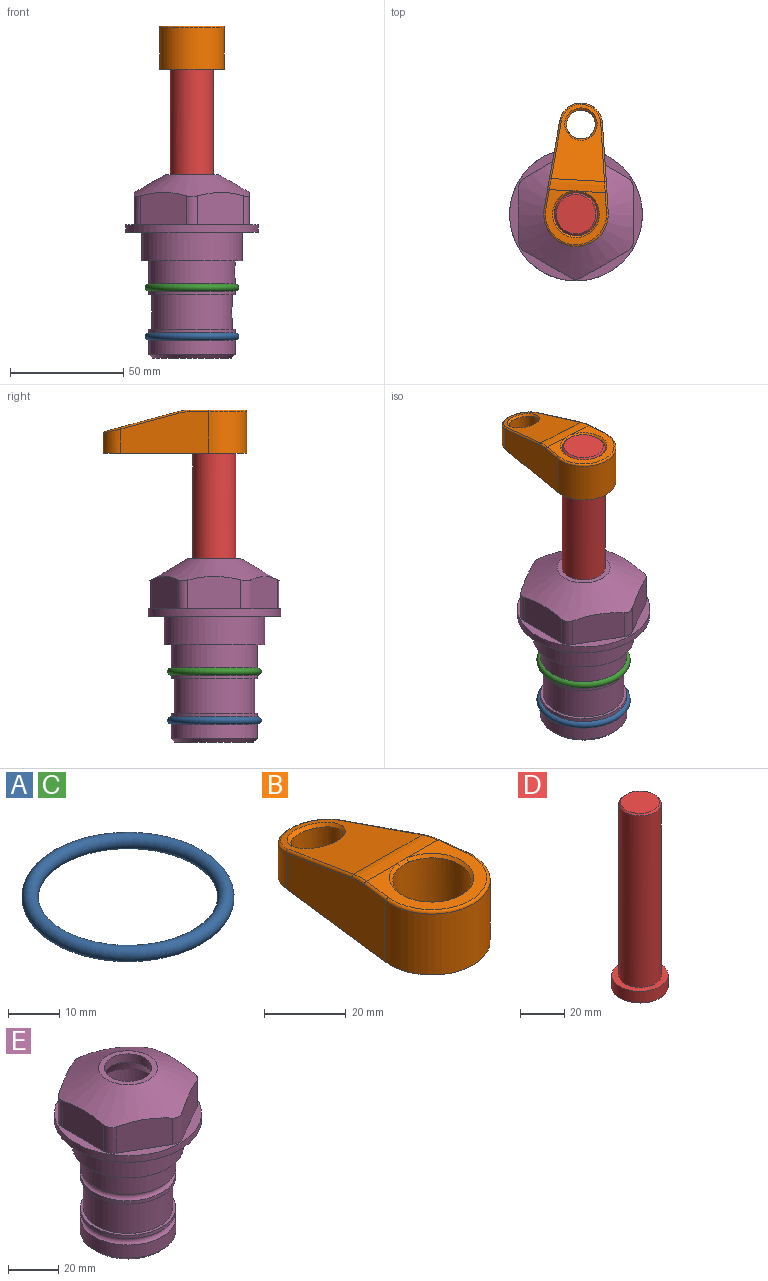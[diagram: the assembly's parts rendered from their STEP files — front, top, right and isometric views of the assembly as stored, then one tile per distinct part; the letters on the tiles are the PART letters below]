
ASSEMBLY  parts=5 mates=4
PART A: 1 faces, bbox 44.7x44.7x3.2 mm
  f0: torus R=19.05mm, axis (0,0,1), area 1193.9mm2
PART B: 31 faces, bbox 31.7x65.5x19.8 mm
  f0: plane 39.12x18.26mm, normal (0.99,0.12,0), area 612.2mm2, adj f1,f4,f7,f11,f13,f15
  f1: cylinder r=9.53mm len=18.91mm, axis (0,0,-1), area 296.1mm2, adj f0,f2,f7,f17
  f2: plane 39.12x18.26mm, normal (-0.99,0.12,0), area 612.2mm2, adj f1,f4,f7,f12,f14,f16
  f3: cylinder r=6.35mm len=12.7mm, axis (0,0,-1), area 362.4mm2, adj f7,f18
  f4: cylinder r=14.29mm len=28.58mm, axis (0,0,-1), area 882.2mm2, adj f0,f2,f7,f10
  f5: cylinder r=9.53mm len=19.05mm, axis (0,0,-1), area 1092.6mm2, adj f7,f19,f20
  f6: plane 26.99x23.69mm, normal (0,0,1), area 216.2mm2, adj f9,f10,f11,f12,f19
  f7: plane 63.5x28.58mm, normal (0,0,-1), area 661.8mm2, adj f0,f1,f2,f3,f4,f5,f22,f23
  f8: plane 33.52x23.6mm, normal (0,0.26,0.97), area 486mm2, adj f9,f15,f16,f17,f18
  f9: cylinder r=19.05mm len=24.72mm, axis (1,0,0), area 120.4mm2, adj f6,f8,f13,f14,f20
  f10: torus R=13.49mm, axis (0,0,1), area 59mm2, adj f4,f6,f11,f12
  f11: cylinder r=0.79mm len=8.67mm, axis (0.12,-0.99,0), area 10.8mm2, adj f0,f6,f10,f13
  f12: cylinder r=0.79mm len=8.67mm, axis (0.12,0.99,0), area 10.8mm2, adj f2,f6,f10,f14
  f13: bspline ~4.95x1.42mm, area 6.1mm2, adj f0,f9,f11,f15
  f14: bspline ~4.95x1.42mm, area 6.1mm2, adj f2,f9,f12,f16
  f15: cylinder r=0.79mm len=25.95mm, axis (0.12,-0.96,0.26), area 32.9mm2, adj f0,f8,f13,f17
  f16: cylinder r=0.79mm len=25.95mm, axis (0.12,0.96,-0.26), area 32.9mm2, adj f2,f8,f14,f17
  f17: bspline ~18.91x8.38mm, area 30mm2, adj f1,f8,f15,f16
  f18: bspline ~14.29x14.29mm, area 48.3mm2, adj f3,f8
  f19: cone r=9.53mm half-angle=45deg, axis (0,0,1), area 66.5mm2, adj f5,f6,f20
  f20: bspline ~3.22x0.96mm, area 3.5mm2, adj f5,f9,f19
  f21: plane 2.75x2.72mm, normal (0,0,-1), area 2.9mm2, adj f23,f25,f28
  f22: plane 23.05x15.88mm, normal (-0.99,-0.12,0), area 323.6mm2, adj f7,f25,f26,f27,f28,f29
  f23: plane 23.05x15.88mm, normal (0.99,-0.12,0), area 323.6mm2, adj f7,f21,f25,f27,f28,f30
  f24: cylinder r=9.53mm len=10.69mm, axis (0,0,-1), area 114.7mm2, adj f7,f27,f29,f30
  f25: cylinder r=12.7mm len=20.59mm, axis (0,0,-1), area 381.1mm2, adj f7,f21,f22,f23,f26,f28
  f26: plane 2.75x2.72mm, normal (0,0,-1), area 2.9mm2, adj f22,f25,f28
  f27: plane 19.72x18.37mm, normal (0,-0.26,-0.97), area 291.8mm2, adj f22,f23,f24,f28,f29,f30
  f28: cylinder r=15.88mm len=19.92mm, axis (1,0,0), area 54.8mm2, adj f21,f22,f23,f25,f26,f27
  f29: cylinder r=1.59mm len=11mm, axis (0,0,-1), area 34.7mm2, adj f7,f22,f24,f27
  f30: cylinder r=1.59mm len=11mm, axis (0,0,-1), area 34.7mm2, adj f7,f23,f24,f27
PART C: same geometry as A
PART D: 6 faces, bbox 25.4x25.4x101.6 mm
  f0: plane 17.46x17.46mm, normal (0,0,1), area 239.5mm2, adj f5
  f1: plane 25.4x25.4mm, normal (0,0,-1), area 506.7mm2, adj f2
  f2: cylinder r=12.7mm len=25.4mm, axis (0,0,1), area 506.7mm2, adj f1,f3
  f3: plane 25.4x25.4mm, normal (0,0,1), area 221.7mm2, adj f2,f4
  f4: cylinder r=9.53mm len=94.46mm, axis (0,0,1), area 5653mm2, adj f3,f5
  f5: cone r=8.73mm half-angle=45deg, axis (0,0,-1), area 64.4mm2, adj f0,f4
PART E: 36 faces, bbox 58.7x58.7x81 mm
  f0: cylinder r=17.78mm len=35.56mm, axis (0,0,1), area 1670.8mm2, adj f23,f24,f31
  f1: cylinder r=19.05mm len=38.1mm, axis (0,0,1), area 1191.9mm2, adj f26,f27,f30
  f2: plane 58.66x58.66mm, normal (0,0,-1), area 1150.6mm2, adj f3,f28
  f3: cylinder r=29.33mm len=58.66mm, axis (0,0,-1), area 585.1mm2, adj f2,f4
  f4: plane 58.66x58.66mm, normal (0,0,1), area 475.9mm2, adj f3,f5,f6,f7,f8,f9,f10,f11
  f5: plane 20.32x14.34mm, normal (-0.5,0.87,0), area 324.4mm2, adj f4,f15,f16,f17
  f6: plane 20.32x14.34mm, normal (0.5,0.87,0), area 324.4mm2, adj f4,f14,f15,f17
  f7: plane 23.48x14.34mm, normal (1,0,0), area 324.4mm2, adj f4,f13,f14,f17
  f8: plane 20.32x14.34mm, normal (0.5,-0.87,0), area 324.4mm2, adj f4,f12,f13,f17
  f9: plane 20.32x14.34mm, normal (-0.5,-0.87,0), area 324.4mm2, adj f4,f11,f12,f17
  f10: plane 23.48x14.34mm, normal (-1,0,0), area 324.4mm2, adj f4,f11,f16,f17
  f11: cylinder r=5.08mm len=12.85mm, axis (0,0,-1), area 67.2mm2, adj f4,f9,f10,f17
  f12: cylinder r=5.08mm len=12.85mm, axis (0,0,-1), area 67.2mm2, adj f4,f8,f9,f17
  f13: cylinder r=5.08mm len=12.85mm, axis (0,0,-1), area 67.2mm2, adj f4,f7,f8,f17
  f14: cylinder r=5.08mm len=12.85mm, axis (0,0,-1), area 67.2mm2, adj f4,f6,f7,f17
  f15: cylinder r=5.08mm len=12.85mm, axis (0,0,-1), area 67.2mm2, adj f4,f5,f6,f17
  f16: cylinder r=5.08mm len=12.85mm, axis (0,0,-1), area 67.2mm2, adj f4,f5,f10,f17
  f17: cone r=11.73mm half-angle=60deg, axis (0,0,-1), area 2071.8mm2, adj f5,f6,f7,f8,f9,f10,f11,f12
  f18: plane 23.46x23.46mm, normal (0,0,1), area 147.4mm2, adj f17,f35
  f19: plane 34.93x34.93mm, normal (0,0,-1), area 958mm2, adj f29
  f20: cylinder r=19.05mm len=38.1mm, axis (0,0,1), area 760.1mm2, adj f21,f29
  f21: torus R=19.05mm, axis (0,0,1), area 565.3mm2, adj f20,f22
  f22: cylinder r=19.05mm len=38.1mm, axis (0,0,1), area 190mm2, adj f21,f23
  f23: plane 38.1x38.1mm, normal (0,0,1), area 146.9mm2, adj f0,f22
  f24: plane 38.1x38.1mm, normal (0,0,-1), area 146.9mm2, adj f0,f25
  f25: cylinder r=19.05mm len=38.1mm, axis (0,0,1), area 190mm2, adj f24,f26
  f26: torus R=19.05mm, axis (0,0,1), area 565.3mm2, adj f1,f25
  f27: plane 44.45x44.45mm, normal (0,0,-1), area 411.7mm2, adj f1,f28
  f28: cylinder r=22.23mm len=44.45mm, axis (0,0,1), area 1773.5mm2, adj f2,f27
  f29: cone r=19.05mm half-angle=45deg, axis (0,0,1), area 257.5mm2, adj f19,f20
  f30: cylinder r=3.17mm len=6.75mm, axis (-1,0,0), area 128mm2, adj f1,f33
  f31: cylinder r=3.17mm len=6.35mm, axis (-1,0,0), area 102.5mm2, adj f0,f33
  f32: plane 25.4x25.4mm, normal (0,0,1), area 506.7mm2, adj f33
  f33: cylinder r=12.7mm len=66.42mm, axis (0,0,-1), area 5236.2mm2, adj f30,f31,f32,f34
  f34: cone r=9.53mm half-angle=30deg, axis (0,0,-1), area 443.4mm2, adj f33,f35
  f35: cylinder r=9.53mm len=19.05mm, axis (0,0,-1), area 240.9mm2, adj f18,f34
PLACE A t=(0,0,-21.59)mm
PLACE B rot(axis=(0,0,-1),3.2deg) t=(0,0,27.55)mm
PLACE C at identity
PLACE D rot(axis=(0,0,-1),3.2deg) t=(0,0,27.55)mm
PLACE E at identity fixed
MATE fastened C.f0 <-> E.f0  axis (0,0,1) through (0,0,-24.51)mm
MATE cylindrical D.f2 <-> E.f0  axis (0,0,-1) through (0,0,-10.55)mm
MATE fastened D.f2 <-> B.f4  axis (0,0,1) through (0,0,91.05)mm
MATE fastened E.f0 <-> A.f0  axis (0,0,1) through (0,0,-46.1)mm
